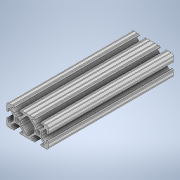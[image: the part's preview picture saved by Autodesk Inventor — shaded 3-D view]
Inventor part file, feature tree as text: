
AUTODESK INVENTOR PART (.ipt)
format: ipt  version: 2020 (Build 240168000, 168)  size: 330,752 bytes
history: native  units: in
note: dims shown in document units (in); Inventor stores cm internally (conversion verified against a paired STEP export)
features: extrude x1, sketch x1
ambient origin geometry x8: Origin, YZ Plane, XZ Plane, XY Plane, X Axis, Y Axis, Z Axis, Center Point
bodies: Solid1 (feature_tree)
feature tree (2):
  extrude  "Extrusion1"  [1 undecoded]
  sketch  "Sketch1"  dims[d0=6.0in d1=0.0in]
note: 1 required parameter value undecoded (feature->parameter linkage not recoverable at this tier; creation-order binding heuristic only, values carry confidence <= 0.55)
